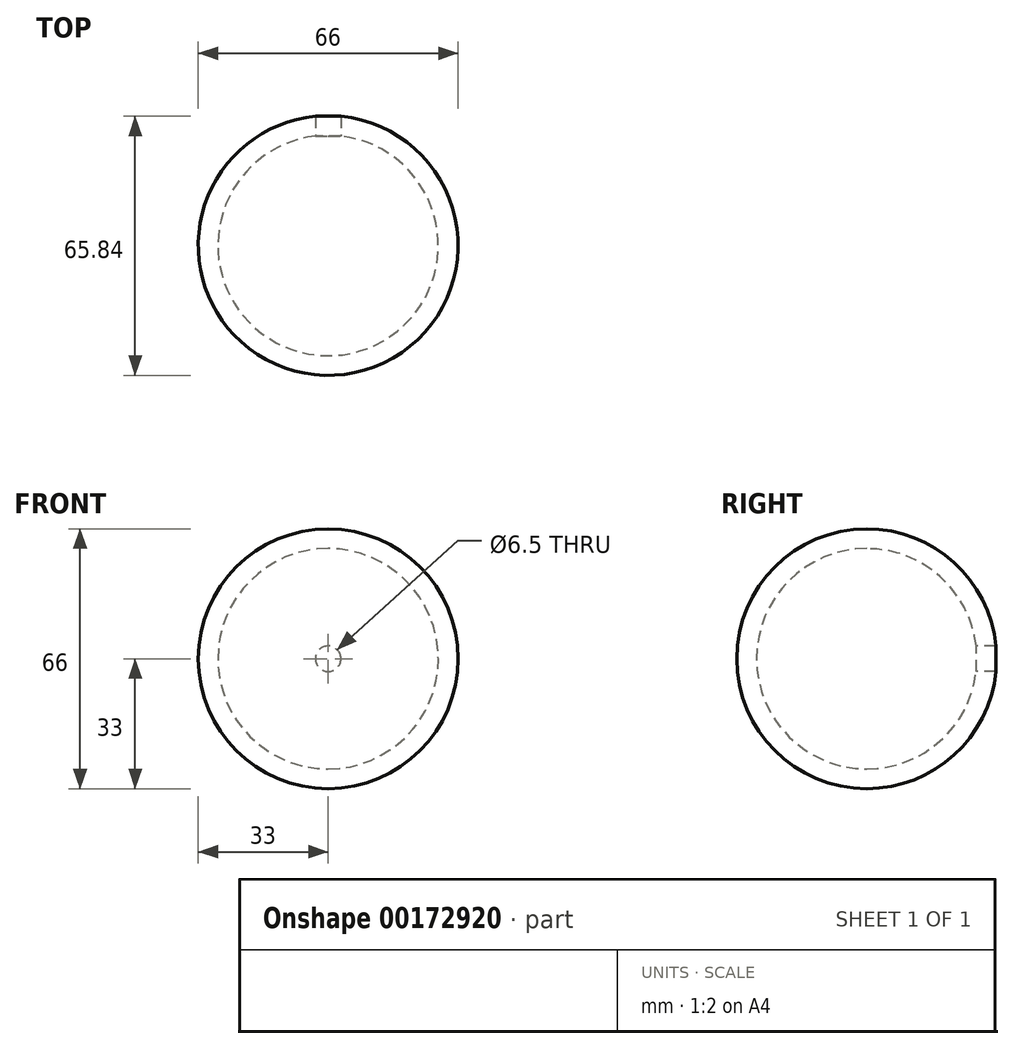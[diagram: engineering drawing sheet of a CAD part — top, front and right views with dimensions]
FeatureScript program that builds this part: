
annotation { "Feature Type Name" : "Feature", "Feature Type Description" : "" }
export const myFeature = defineFeature(function(context is Context, id is Id, definition is map)
    precondition{}
    {
        {
            var Q0;
            Q0=qCreatedBy(makeId("Front.planeOp"),FACE);
            var sketch = newSketch(context, id + "F0", { "sketchPlane" : qUnion([Q0])});
            skArc(sketch, "E0", {"start": v(0, 33) * mm, "mid": v(-33, 0) * mm, "end": v(0, -33) * mm});
            skArc(sketch, "E1", {"start": v(0, 28) * mm, "mid": v(-28, 0) * mm, "end": v(0, -28) * mm});
            skLineSegment(sketch, "E2", {"start": v(0, 33) * mm, "end": v(0, 28) * mm});
            skLineSegment(sketch, "E3.trimOffspring", {"start": v(0, -28) * mm, "end": v(0, -33) * mm});
            skSolve(sketch);
        }
        {
            var Q0;
            Q0=makeQuery(id+"F0.imprint","IMPRINT",FACE,{"disambiguationData":[TD([[makeQuery(id+"F0.imprint","IMPRINT",EDGE,{"derivedFrom":sQuery(id+"F0.wireOp",EDGE,"E0")}),1.0]])]});
            var Q1;
            Q1=sQuery(id+"F0.wireOp",EDGE,"E2");
            revolve(context, id + "F1", {"entities" : qUnion([Q0]), "axis" : qUnion([Q1]), "revolveType" : RevolveType.FULL});
        }
        {
            var Q0;
            Q0=qCreatedBy(makeId("Front.planeOp"),FACE);
            var sketch = newSketch(context, id + "F2", { "sketchPlane" : qUnion([Q0])});
            skCircle(sketch, "E4", {"center": v(0, 0) * mm, "radius": 3.25 * mm});
            skSolve(sketch);
        }
        {
            var Q0;
            Q0=sQuery(id+"F2.wireOp",VERTEX,"E4.center");
            var Q1;
            Q1=makeQuery(id+"F1.opRevolve","SWEPT_BODY",BODY,{"disambiguationData":[OSD([sQuery(id+"F0.wireOp",EDGE,"E0"),sQuery(id+"F0.wireOp",EDGE,"E1"),sQuery(id+"F0.wireOp",EDGE,"E2"),sQuery(id+"F0.wireOp",EDGE,"E3.trimOffspring")])]});
            hole(context, id + "F3", {"style" : HoleStyle.SIMPLE, "endStyle" : HoleEndStyle.BLIND, "holeDiameter" : 6.5 * mm, "holeDepth" : 33 * mm, "startFromSketch" : true, "locations" : qUnion([Q0]), "scope" : qUnion([Q1])});
        }
    });
